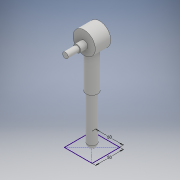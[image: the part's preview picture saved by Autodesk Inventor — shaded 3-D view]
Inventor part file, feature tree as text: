
AUTODESK INVENTOR PART (.ipt)
format: ipt  version: 2018 (Build 220112000, 112)  size: 146,432 bytes
history: native  units: mm
features: sketch x8, extrude x5, other x3, fillet x1
ambient origin geometry x8: Origin, YZ Plane, XZ Plane, XY Plane, X Axis, Y Axis, Z Axis, Center Point
bodies: Body1 (feature_tree)
feature tree (17):
  other  "ソリッド1"
  extrude  "押し出し1"  Depth=16.0mm
  sketch  "スケッチ2"
  extrude  "押し出し2"  Depth=88.47mm TaperAngle=0.0deg
  fillet  "フィレット1"  Radius=8.0mm
  extrude  "押し出し3"  Depth=21.0mm
  other  "作業平面1"
  sketch  "スケッチ5"
  other  "作業平面2"
  extrude  "押し出し4"  Depth=82.0mm TaperAngle=0.0deg
  extrude  "押し出し5"  Depth=40.0mm
  sketch  "スケッチ11"
  sketch  "スケッチ1"
  sketch  "スケッチ3"
  sketch  "スケッチ4"
  sketch  "スケッチ8"
  sketch  "スケッチ9"
